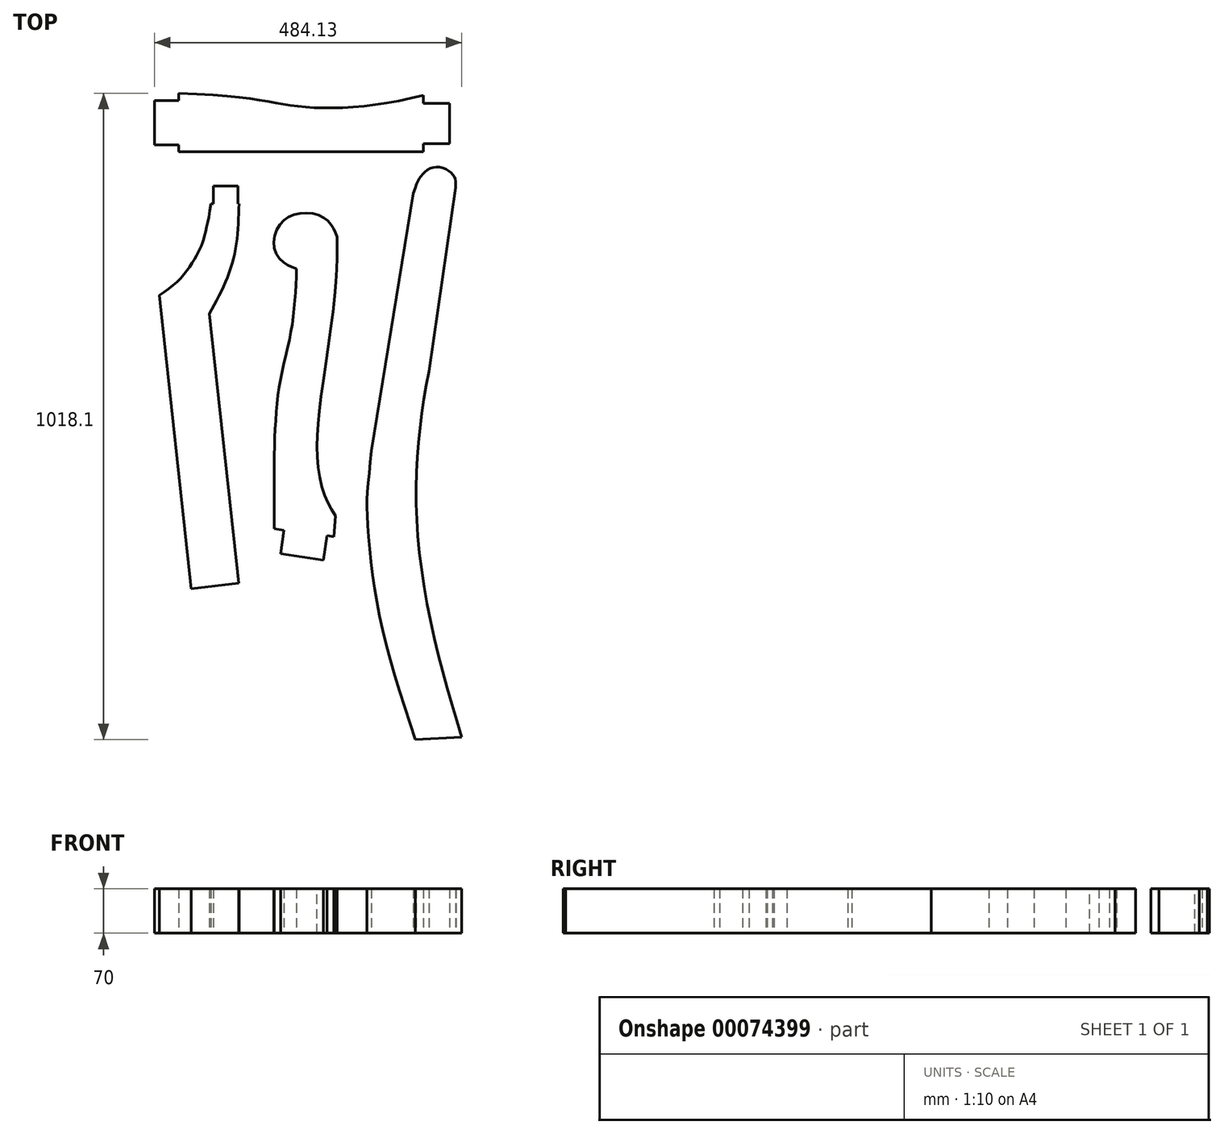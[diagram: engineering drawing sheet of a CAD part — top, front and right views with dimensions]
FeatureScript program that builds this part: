
annotation { "Feature Type Name" : "Feature", "Feature Type Description" : "" }
export const myFeature = defineFeature(function(context is Context, id is Id, definition is map)
    precondition{}
    {
        {
            var Q0;
            Q0=qCreatedBy(makeId("Top.planeOp"),FACE);
            var sketch = newSketch(context, id + "F0", { "sketchPlane" : qUnion([Q0])});
            skLineSegment(sketch, "E0.left", {"start": v(0, 0) * mm, "end": v(0, -88.9) * mm});
            skLineSegment(sketch, "E1", {"start": v(-41.28, -4.38) * mm, "end": v(-41.28, -17.08) * mm});
            skLineSegment(sketch, "E2", {"start": v(-41.27, -17.08) * mm, "end": v(0, -17.08) * mm});
            skLineSegment(sketch, "E3", {"start": v(0, -80.84) * mm, "end": v(-41.27, -80.84) * mm});
            skLineSegment(sketch, "E4", {"start": v(-41.28, -80.84) * mm, "end": v(-41.28, -93.54) * mm});
            skLineSegment(sketch, "E5", {"start": v(-426.72, -93.54) * mm, "end": v(-426.72, -82.4) * mm});
            skLineSegment(sketch, "E6", {"start": v(-426.72, -82.4) * mm, "end": v(-464.82, -82.4) * mm});
            skLineSegment(sketch, "E7", {"start": v(-464.82, -12.56) * mm, "end": v(-426.72, -12.56) * mm});
            skLineSegment(sketch, "E8", {"start": v(-426.72, -12.56) * mm, "end": v(-426.72, -1.25) * mm});
            skLineSegment(sketch, "E9", {"start": v(-464.82, -12.56) * mm, "end": v(-464.82, -82.4) * mm});
            skLineSegment(sketch, "E10", {"start": v(-426.72, -93.54) * mm, "end": v(-41.28, -93.54) * mm});
            skFitSpline(sketch, "E11", {"points": [v(-426.72, -1.25) * mm, v(-231.55, -22.66) * mm, v(-41.27, -4.38) * mm], "startDerivative": vector(713.67, -21.46) * mm, "endDerivative": vector(452.43, 118.43) * mm});
            skSolve(sketch);
        }
        {
            var Q0;
            {var subQ5=sQuery(id+"F0.wireOp",EDGE,"E1");Q0=makeQuery(id+"F0.imprint","IMPRINT",FACE,{"disambiguationData":[TD([[makeQuery(id+"F0.imprint","IMPRINT",EDGE,{"derivedFrom":subQ5}),-1.0]])]});}
            extrude(context, id + "F1", {"entities" : qUnion([Q0]), "depth" : 70 * mm});
        }
        {
            var Q0;
            Q0=qCreatedBy(makeId("Top.planeOp"),FACE);
            var sketch = newSketch(context, id + "F2", { "sketchPlane" : qUnion([Q0])});
            skLineSegment(sketch, "E12", {"start": v(-406.94, -781.77) * mm, "end": v(-331.9, -773.08) * mm});
            skLineSegment(sketch, "E13", {"start": v(-331.9, -773.08) * mm, "end": v(-378.01, -349.05) * mm});
            skLineSegment(sketch, "E14", {"start": v(-457.17, -319.3) * mm, "end": v(-406.94, -781.77) * mm});
            skLineSegment(sketch, "E15", {"start": v(-375.46, -175.21) * mm, "end": v(-371.56, -175.21) * mm});
            skLineSegment(sketch, "E16", {"start": v(-371.56, -175.21) * mm, "end": v(-371.56, -147.35) * mm});
            skLineSegment(sketch, "E17", {"start": v(-371.56, -147.35) * mm, "end": v(-333.27, -147.35) * mm});
            skLineSegment(sketch, "E18", {"start": v(-333.27, -147.35) * mm, "end": v(-333.27, -175.21) * mm});
            skFitSpline(sketch, "E19", {"points": [v(-457.17, -319.3) * mm, v(-396.38, -253.23) * mm, v(-375.46, -175.21) * mm], "startDerivative": vector(186.56, 106.2) * mm, "endDerivative": vector(45.96, 270.5) * mm});
            skFitSpline(sketch, "E20", {"points": [v(-378.01, -349.05) * mm, v(-340.8, -264.71) * mm, v(-331.45, -175.21) * mm], "startDerivative": vector(87.83, 164.54) * mm, "endDerivative": vector(5.13, 183.17) * mm});
            skLineSegment(sketch, "E21", {"start": v(-333.27, -175.21) * mm, "end": v(-331.45, -175.21) * mm});
            skSolve(sketch);
        }
        {
            var Q0;
            Q0=qCreatedBy(makeId("Top.planeOp"),FACE);
            var sketch = newSketch(context, id + "F3", { "sketchPlane" : qUnion([Q0])});
            skLineSegment(sketch, "E22", {"start": v(-337.45, -228.04) * mm, "end": v(-335.62, -228.04) * mm});
            skLineSegment(sketch, "E23", {"start": v(-192.57, -698.1) * mm, "end": v(-182.25, -699.65) * mm});
            skLineSegment(sketch, "E24", {"start": v(-192.57, -698.1) * mm, "end": v(-198.35, -736.96) * mm});
            skLineSegment(sketch, "E25", {"start": v(-198.35, -736.96) * mm, "end": v(-266.06, -726.88) * mm});
            skLineSegment(sketch, "E26", {"start": v(-266.06, -726.88) * mm, "end": v(-260.54, -689.8) * mm});
            skLineSegment(sketch, "E27", {"start": v(-260.54, -689.8) * mm, "end": v(-276.07, -687.5) * mm});
            skLineSegment(sketch, "E28", {"start": v(-276.07, -687.5) * mm, "end": v(-276.07, -571.23) * mm});
            skFitSpline(sketch, "E29", {"points": [v(-276.07, -571.23) * mm, v(-268.1, -464.08) * mm, v(-248.58, -371.21) * mm, v(-240.78, -277.56) * mm], "startDerivative": vector(10.4, 314.89) * mm, "endDerivative": vector(12.15, 290.44) * mm});
            skFitSpline(sketch, "E30", {"points": [v(-240.78, -277.56) * mm, v(-261.02, -267.97) * mm, v(-276.5, -242.6) * mm, v(-267.63, -209.05) * mm, v(-240.78, -191.32) * mm, v(-204.7, -193.93) * mm, v(-185.59, -209.57) * mm, v(-176.72, -227.65) * mm], "startDerivative": vector(-163.97, 54.67) * mm, "endDerivative": vector(61.29, -153.8) * mm});
            skFitSpline(sketch, "E31", {"points": [v(-176.72, -227.65) * mm, v(-179.7, -311.9) * mm, v(-202.9, -485.37) * mm, v(-208.1, -574.5) * mm, v(-197.05, -632.69) * mm, v(-179.5, -667.2) * mm], "startDerivative": vector(2.33, -368.94) * mm, "endDerivative": vector(142.32, -233.4) * mm});
            skLineSegment(sketch, "E32", {"start": v(-179.5, -667.14) * mm, "end": v(-182.25, -699.65) * mm});
            skSolve(sketch);
        }
        {
            var Q0;
            Q0=qCreatedBy(makeId("Top.planeOp"),FACE);
            var sketch = newSketch(context, id + "F4", { "sketchPlane" : qUnion([Q0])});
            skLineSegment(sketch, "E33", {"start": v(-53.79, -1019.35) * mm, "end": v(19.3, -1015.5) * mm});
            skFitSpline(sketch, "E34", {"points": [v(19.3, -1015.5) * mm, v(-24.62, -855.57) * mm, v(-50.2, -691.81) * mm, v(-48.84, -554.78) * mm, v(-31.9, -439.38) * mm], "startDerivative": vector(-177.7, 592.19) * mm, "endDerivative": vector(108.58, 505.98) * mm});
            skLineSegment(sketch, "E35", {"start": v(-31.9, -439.38) * mm, "end": v(9.86, -150.1) * mm});
            skFitSpline(sketch, "E36", {"points": [v(9.86, -150.1) * mm, v(9.86, -140.34) * mm, v(5.62, -129.53) * mm, v(-10.47, -118.94) * mm, v(-30.4, -119.73) * mm, v(-45.2, -132.5) * mm, v(-56.6, -158.7) * mm], "startDerivative": vector(4.72, 77.9) * mm, "endDerivative": vector(-68.22, -219.5) * mm});
            skLineSegment(sketch, "E37", {"start": v(-56.6, -158.7) * mm, "end": v(-122.65, -564.76) * mm});
            skFitSpline(sketch, "E38", {"points": [v(-122.65, -564.76) * mm, v(-129, -628.7) * mm, v(-129.51, -664.83) * mm, v(-122.65, -747.32) * mm, v(-101.16, -863.37) * mm, v(-53.79, -1019.35) * mm], "startDerivative": vector(-45.03, -408.74) * mm, "endDerivative": vector(192.96, -589.93) * mm});
            skSolve(sketch);
        }
        {
            var Q0;
            Q0=makeQuery(id+"F4.imprint","IMPRINT",FACE,{"disambiguationData":[TD([[makeQuery(id+"F4.imprint","IMPRINT",EDGE,{"derivedFrom":sQuery(id+"F4.wireOp",EDGE,"E33")}),1.0]])]});
            extrude(context, id + "F5", {"entities" : qUnion([Q0]), "depth" : 70 * mm});
        }
        {
            var Q0;
            Q0 = qSketchRegion(id + "F2", true);
            var Q1;
            Q1=makeQuery(id+"F2.imprint","IMPRINT",FACE,{"disambiguationData":[TD([[makeQuery(id+"F2.imprint","IMPRINT",EDGE,{"derivedFrom":sQuery(id+"F2.wireOp",EDGE,"E12")}),1.0]])]});
            extrude(context, id + "F6", {"entities" : qUnion([Q0, Q1]), "depth" : 70 * mm});
        }
        {
            var Q0;
            Q0 = qSketchRegion(id + "F3", true);
            extrude(context, id + "F7", {"entities" : qUnion([Q0]), "depth" : 70 * mm});
        }
    });
